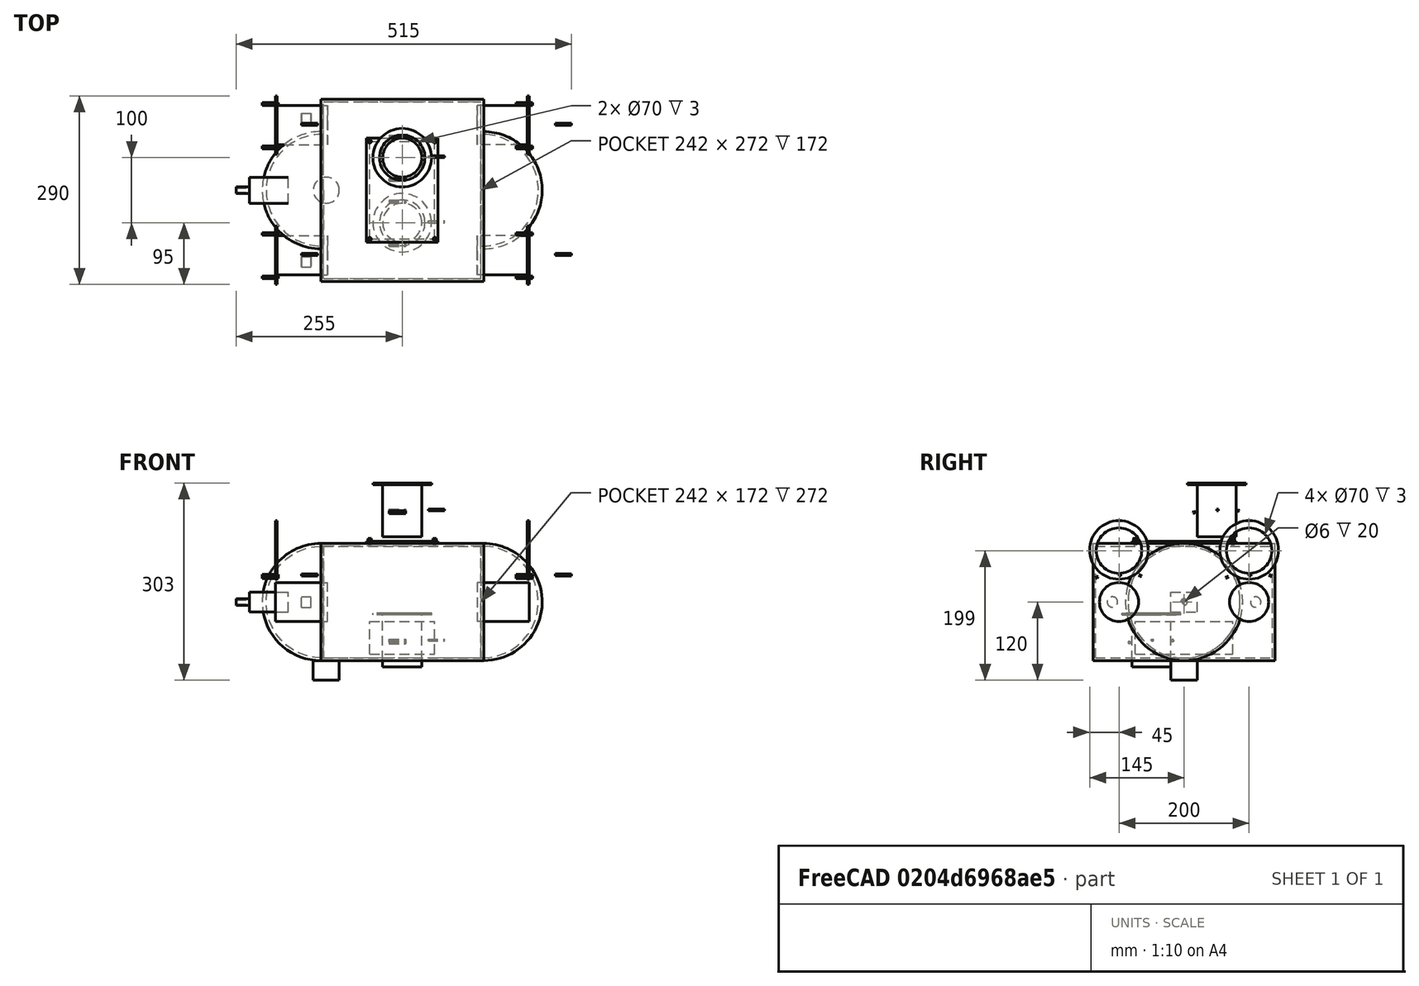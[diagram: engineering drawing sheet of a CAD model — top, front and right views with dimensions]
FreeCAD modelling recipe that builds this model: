
FCSTD DOCUMENT  (FreeCAD 0.19R)
Label: fishing_drone_advanced
License: All rights reserved
LicenseURL: http://en.wikipedia.org/wiki/All_rights_reserved
objects: Part::Cylinder×27, Part::Box×24, Part::MultiFuse×10, Part::Cut×8, Part::Sphere×4
note: 73 computed .brp shape members not serialized (recipe doc carries the construction recipe); baked Part::Feature solids carry a one-line shape summary decoded from their .brp

FEATURE [Part::Box] CenterBody
  AttacherType = Attacher::AttachEngine3D
  Height = 180
  Length = 250
  Placement = pos=(-125,-140,-90) rot=(0,0,1;0rad)
  Width = 280
FEATURE [Part::Sphere] Nose
  Angle1 = -90
  Angle2 = 90
  Angle3 = 360
  AttacherType = Attacher::AttachEngine3D
  Placement = pos=(-125,0,0) rot=(0,0,1;0rad)
  Radius = 90
FEATURE [Part::Sphere] Tail
  Angle1 = -90
  Angle2 = 90
  Angle3 = 360
  AttacherType = Attacher::AttachEngine3D
  Placement = pos=(125,0,0) rot=(0,0,1;0rad)
  Radius = 90
FEATURE [Part::MultiFuse] BodyOuter
  Shapes = -> [CenterBody,Nose,Tail]
FEATURE [Part::Box] CenterInner
  AttacherType = Attacher::AttachEngine3D
  Height = 172
  Length = 242
  Placement = pos=(-121,-136,-86) rot=(0,0,1;0rad)
  Width = 272
FEATURE [Part::Sphere] NoseInner
  Angle1 = -90
  Angle2 = 90
  Angle3 = 360
  AttacherType = Attacher::AttachEngine3D
  Placement = pos=(-123,0,0) rot=(0,0,1;0rad)
  Radius = 86
FEATURE [Part::Sphere] TailInner
  Angle1 = -90
  Angle2 = 90
  Angle3 = 360
  AttacherType = Attacher::AttachEngine3D
  Placement = pos=(123,0,0) rot=(0,0,1;0rad)
  Radius = 86
FEATURE [Part::MultiFuse] BodyInner
  Shapes = -> [CenterInner,NoseInner,TailInner]
FEATURE [Part::Cut] HollowBody
  Base = -> BodyOuter
  Tool = -> BodyInner
FEATURE [Part::Cylinder] MotorHousing_FrontLeft
  Angle = 360
  AttacherType = Attacher::AttachEngine3D
  Height = 80
  Placement = pos=(-195,100,0) rot=(0,1,0;1.5708rad)
  Radius = 30
FEATURE [Part::Cylinder] GuardOuter_FrontLeft
  Angle = 360
  AttacherType = Attacher::AttachEngine3D
  Height = 3
  Placement = pos=(-195,100,80) rot=(0,1,0;1.5708rad)
  Radius = 45
FEATURE [Part::Cylinder] GuardInner_FrontLeft
  Angle = 360
  AttacherType = Attacher::AttachEngine3D
  Height = 5
  Placement = pos=(-195,100,79) rot=(0,1,0;1.5708rad)
  Radius = 35
FEATURE [Part::Cut] GuardRing_FrontLeft
  Base = -> GuardOuter_FrontLeft
  Tool = -> GuardInner_FrontLeft
FEATURE [Part::Box] Strut_FrontLeft_0
  AttacherType = Attacher::AttachEngine3D
  Height = 3
  Length = 25
  Placement = pos=(-155,100,40) rot=(0,0,1;0rad)
  Width = 3
FEATURE [Part::Box] Strut_FrontLeft_1
  AttacherType = Attacher::AttachEngine3D
  Height = 3
  Length = 25
  Placement = pos=(-215,134.641,40) rot=(1,0,0;2.0944rad)
  Width = 3
FEATURE [Part::Box] Strut_FrontLeft_2
  AttacherType = Attacher::AttachEngine3D
  Height = 3
  Length = 25
  Placement = pos=(-215,65.359,40) rot=(1,0,0;4.18879rad)
  Width = 3
FEATURE [Part::MultiFuse] ThrusterAssembly_FrontLeft
  Shapes = -> [MotorHousing_FrontLeft,GuardRing_FrontLeft,Strut_FrontLeft_0,Strut_FrontLeft_1,Strut_FrontLeft_2]
FEATURE [Part::Cylinder] MotorHousing_FrontRight
  Angle = 360
  AttacherType = Attacher::AttachEngine3D
  Height = 80
  Placement = pos=(-195,-100,0) rot=(0,1,0;1.5708rad)
  Radius = 30
FEATURE [Part::Cylinder] GuardOuter_FrontRight
  Angle = 360
  AttacherType = Attacher::AttachEngine3D
  Height = 3
  Placement = pos=(-195,-100,80) rot=(0,1,0;1.5708rad)
  Radius = 45
FEATURE [Part::Cylinder] GuardInner_FrontRight
  Angle = 360
  AttacherType = Attacher::AttachEngine3D
  Height = 5
  Placement = pos=(-195,-100,79) rot=(0,1,0;1.5708rad)
  Radius = 35
FEATURE [Part::Cut] GuardRing_FrontRight
  Base = -> GuardOuter_FrontRight
  Tool = -> GuardInner_FrontRight
FEATURE [Part::Box] Strut_FrontRight_0
  AttacherType = Attacher::AttachEngine3D
  Height = 3
  Length = 25
  Placement = pos=(-155,-100,40) rot=(0,0,1;0rad)
  Width = 3
FEATURE [Part::Box] Strut_FrontRight_1
  AttacherType = Attacher::AttachEngine3D
  Height = 3
  Length = 25
  Placement = pos=(-215,-65.359,40) rot=(1,0,0;2.0944rad)
  Width = 3
FEATURE [Part::Box] Strut_FrontRight_2
  AttacherType = Attacher::AttachEngine3D
  Height = 3
  Length = 25
  Placement = pos=(-215,-134.641,40) rot=(1,0,0;4.18879rad)
  Width = 3
FEATURE [Part::MultiFuse] ThrusterAssembly_FrontRight
  Shapes = -> [MotorHousing_FrontRight,GuardRing_FrontRight,Strut_FrontRight_0,Strut_FrontRight_1,Strut_FrontRight_2]
FEATURE [Part::Cylinder] MotorHousing_RearLeft
  Angle = 360
  AttacherType = Attacher::AttachEngine3D
  Height = 80
  Placement = pos=(195,100,0) rot=(0,1,0;-1.5708rad)
  Radius = 30
FEATURE [Part::Cylinder] GuardOuter_RearLeft
  Angle = 360
  AttacherType = Attacher::AttachEngine3D
  Height = 3
  Placement = pos=(195,100,80) rot=(0,1,0;-1.5708rad)
  Radius = 45
FEATURE [Part::Cylinder] GuardInner_RearLeft
  Angle = 360
  AttacherType = Attacher::AttachEngine3D
  Height = 5
  Placement = pos=(195,100,79) rot=(0,1,0;-1.5708rad)
  Radius = 35
FEATURE [Part::Cut] GuardRing_RearLeft
  Base = -> GuardOuter_RearLeft
  Tool = -> GuardInner_RearLeft
FEATURE [Part::Box] Strut_RearLeft_0
  AttacherType = Attacher::AttachEngine3D
  Height = 3
  Length = 25
  Placement = pos=(235,100,40) rot=(0,0,1;0rad)
  Width = 3
FEATURE [Part::Box] Strut_RearLeft_1
  AttacherType = Attacher::AttachEngine3D
  Height = 3
  Length = 25
  Placement = pos=(175,134.641,40) rot=(1,0,0;2.0944rad)
  Width = 3
FEATURE [Part::Box] Strut_RearLeft_2
  AttacherType = Attacher::AttachEngine3D
  Height = 3
  Length = 25
  Placement = pos=(175,65.359,40) rot=(1,0,0;4.18879rad)
  Width = 3
FEATURE [Part::MultiFuse] ThrusterAssembly_RearLeft
  Shapes = -> [MotorHousing_RearLeft,GuardRing_RearLeft,Strut_RearLeft_0,Strut_RearLeft_1,Strut_RearLeft_2]
FEATURE [Part::Cylinder] MotorHousing_RearRight
  Angle = 360
  AttacherType = Attacher::AttachEngine3D
  Height = 80
  Placement = pos=(195,-100,0) rot=(0,1,0;-1.5708rad)
  Radius = 30
FEATURE [Part::Cylinder] GuardOuter_RearRight
  Angle = 360
  AttacherType = Attacher::AttachEngine3D
  Height = 3
  Placement = pos=(195,-100,80) rot=(0,1,0;-1.5708rad)
  Radius = 45
FEATURE [Part::Cylinder] GuardInner_RearRight
  Angle = 360
  AttacherType = Attacher::AttachEngine3D
  Height = 5
  Placement = pos=(195,-100,79) rot=(0,1,0;-1.5708rad)
  Radius = 35
FEATURE [Part::Cut] GuardRing_RearRight
  Base = -> GuardOuter_RearRight
  Tool = -> GuardInner_RearRight
FEATURE [Part::Box] Strut_RearRight_0
  AttacherType = Attacher::AttachEngine3D
  Height = 3
  Length = 25
  Placement = pos=(235,-100,40) rot=(0,0,1;0rad)
  Width = 3
FEATURE [Part::Box] Strut_RearRight_1
  AttacherType = Attacher::AttachEngine3D
  Height = 3
  Length = 25
  Placement = pos=(175,-65.359,40) rot=(1,0,0;2.0944rad)
  Width = 3
FEATURE [Part::Box] Strut_RearRight_2
  AttacherType = Attacher::AttachEngine3D
  Height = 3
  Length = 25
  Placement = pos=(175,-134.641,40) rot=(1,0,0;4.18879rad)
  Width = 3
FEATURE [Part::MultiFuse] ThrusterAssembly_RearRight
  Shapes = -> [MotorHousing_RearRight,GuardRing_RearRight,Strut_RearRight_0,Strut_RearRight_1,Strut_RearRight_2]
FEATURE [Part::Cylinder] MotorHousing_TopCenter
  Angle = 360
  AttacherType = Attacher::AttachEngine3D
  Height = 80
  Placement = pos=(0,50,100) rot=(0,0,1;0rad)
  Radius = 30
FEATURE [Part::Cylinder] GuardOuter_TopCenter
  Angle = 360
  AttacherType = Attacher::AttachEngine3D
  Height = 3
  Placement = pos=(0,50,180) rot=(0,0,1;0rad)
  Radius = 45
FEATURE [Part::Cylinder] GuardInner_TopCenter
  Angle = 360
  AttacherType = Attacher::AttachEngine3D
  Height = 5
  Placement = pos=(0,50,179) rot=(0,0,1;0rad)
  Radius = 35
FEATURE [Part::Cut] GuardRing_TopCenter
  Base = -> GuardOuter_TopCenter
  Tool = -> GuardInner_TopCenter
FEATURE [Part::Box] Strut_TopCenter_0
  AttacherType = Attacher::AttachEngine3D
  Height = 3
  Length = 25
  Placement = pos=(40,50,140) rot=(0,0,1;0rad)
  Width = 3
FEATURE [Part::Box] Strut_TopCenter_1
  AttacherType = Attacher::AttachEngine3D
  Height = 3
  Length = 25
  Placement = pos=(-20,84.641,140) rot=(1,0,0;2.0944rad)
  Width = 3
FEATURE [Part::Box] Strut_TopCenter_2
  AttacherType = Attacher::AttachEngine3D
  Height = 3
  Length = 25
  Placement = pos=(-20,15.359,140) rot=(1,0,0;4.18879rad)
  Width = 3
FEATURE [Part::MultiFuse] ThrusterAssembly_TopCenter
  Shapes = -> [MotorHousing_TopCenter,GuardRing_TopCenter,Strut_TopCenter_0,Strut_TopCenter_1,Strut_TopCenter_2]
FEATURE [Part::Cylinder] MotorHousing_BottomCenter
  Angle = 360
  AttacherType = Attacher::AttachEngine3D
  Height = 80
  Placement = pos=(0,-50,-100) rot=(0,0,1;0rad)
  Radius = 30
FEATURE [Part::Cylinder] GuardOuter_BottomCenter
  Angle = 360
  AttacherType = Attacher::AttachEngine3D
  Height = 3
  Placement = pos=(0,-50,-20) rot=(0,0,1;0rad)
  Radius = 45
FEATURE [Part::Cylinder] GuardInner_BottomCenter
  Angle = 360
  AttacherType = Attacher::AttachEngine3D
  Height = 5
  Placement = pos=(0,-50,-21) rot=(0,0,1;0rad)
  Radius = 35
FEATURE [Part::Cut] GuardRing_BottomCenter
  Base = -> GuardOuter_BottomCenter
  Tool = -> GuardInner_BottomCenter
FEATURE [Part::Box] Strut_BottomCenter_0
  AttacherType = Attacher::AttachEngine3D
  Height = 3
  Length = 25
  Placement = pos=(40,-50,-60) rot=(0,0,1;0rad)
  Width = 3
FEATURE [Part::Box] Strut_BottomCenter_1
  AttacherType = Attacher::AttachEngine3D
  Height = 3
  Length = 25
  Placement = pos=(-20,-15.359,-60) rot=(1,0,0;2.0944rad)
  Width = 3
FEATURE [Part::Box] Strut_BottomCenter_2
  AttacherType = Attacher::AttachEngine3D
  Height = 3
  Length = 25
  Placement = pos=(-20,-84.641,-60) rot=(1,0,0;4.18879rad)
  Width = 3
FEATURE [Part::MultiFuse] ThrusterAssembly_BottomCenter
  Shapes = -> [MotorHousing_BottomCenter,GuardRing_BottomCenter,Strut_BottomCenter_0,Strut_BottomCenter_1,Strut_BottomCenter_2]
FEATURE [Part::Box] BatteryBay
  AttacherType = Attacher::AttachEngine3D
  Height = 50
  Length = 100
  Placement = pos=(-50,-75,-80) rot=(0,0,1;0rad)
  Width = 150
FEATURE [Part::Box] BatteryCover
  AttacherType = Attacher::AttachEngine3D
  Height = 3
  Length = 110
  Placement = pos=(-55,-80,90) rot=(0,0,1;0rad)
  Width = 160
FEATURE [Part::Cylinder] ScrewHole_0
  Angle = 360
  AttacherType = Attacher::AttachEngine3D
  Height = 10
  Placement = pos=(-50,-75,88) rot=(0,0,1;0rad)
  Radius = 2.5
FEATURE [Part::Cylinder] ScrewHole_1
  Angle = 360
  AttacherType = Attacher::AttachEngine3D
  Height = 10
  Placement = pos=(-50,75,88) rot=(0,0,1;0rad)
  Radius = 2.5
FEATURE [Part::Cylinder] ScrewHole_2
  Angle = 360
  AttacherType = Attacher::AttachEngine3D
  Height = 10
  Placement = pos=(50,-75,88) rot=(0,0,1;0rad)
  Radius = 2.5
FEATURE [Part::Cylinder] ScrewHole_3
  Angle = 360
  AttacherType = Attacher::AttachEngine3D
  Height = 10
  Placement = pos=(50,75,88) rot=(0,0,1;0rad)
  Radius = 2.5
FEATURE [Part::Box] ReleaseMechanism
  AttacherType = Attacher::AttachEngine3D
  Height = 30
  Length = 60
  Placement = pos=(-235,-20,-15) rot=(0,0,1;0rad)
  Width = 40
FEATURE [Part::Box] ServoMount
  AttacherType = Attacher::AttachEngine3D
  Height = 20
  Length = 25
  Placement = pos=(-215,-7.5,-10) rot=(0,0,1;0rad)
  Width = 15
FEATURE [Part::Cylinder] LineGuideOuter
  Angle = 360
  AttacherType = Attacher::AttachEngine3D
  Height = 40
  Placement = pos=(-255,0,0) rot=(0,1,0;1.5708rad)
  Radius = 5
FEATURE [Part::Cylinder] LineGuideInner
  Angle = 360
  AttacherType = Attacher::AttachEngine3D
  Height = 45
  Placement = pos=(-257,0,0) rot=(0,1,0;1.5708rad)
  Radius = 3
FEATURE [Part::Cut] LineGuideTube
  Base = -> LineGuideOuter
  Tool = -> LineGuideInner
FEATURE [Part::MultiFuse] ReleaseAssembly
  Shapes = -> [ReleaseMechanism,ServoMount,LineGuideTube]
FEATURE [Part::Cylinder] CameraGimbal
  Angle = 360
  AttacherType = Attacher::AttachEngine3D
  Height = 30
  Placement = pos=(-116.667,0,-120) rot=(0,0,1;0rad)
  Radius = 20
FEATURE [Part::Cylinder] LED_Left
  Angle = 360
  AttacherType = Attacher::AttachEngine3D
  Height = 15
  Placement = pos=(-155,110,0) rot=(0,1,0;1.5708rad)
  Radius = 8
FEATURE [Part::Cylinder] LED_Right
  Angle = 360
  AttacherType = Attacher::AttachEngine3D
  Height = 15
  Placement = pos=(-155,-110,0) rot=(0,1,0;1.5708rad)
  Radius = 8
FEATURE [Part::MultiFuse] CameraAssembly
  Shapes = -> [CameraGimbal,LED_Left,LED_Right]
